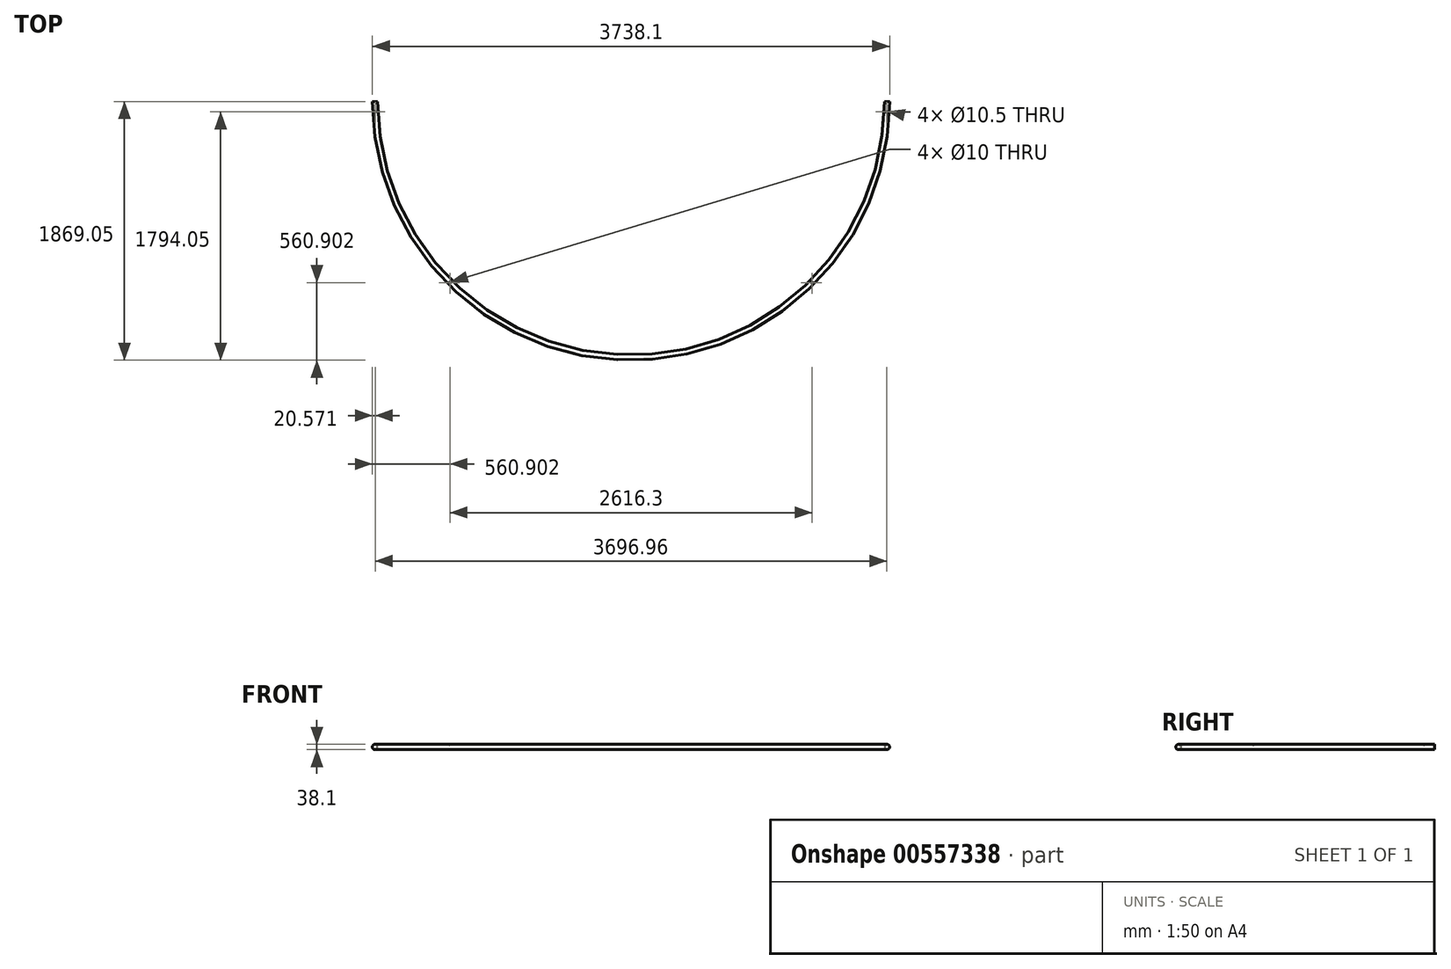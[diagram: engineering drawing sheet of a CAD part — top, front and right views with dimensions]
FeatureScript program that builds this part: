
annotation { "Feature Type Name" : "Feature", "Feature Type Description" : "" }
export const myFeature = defineFeature(function(context is Context, id is Id, definition is map)
    precondition{}
    {
        {
            var Q0;
            Q0=qCreatedBy(makeId("Front.planeOp"),FACE);
            var sketch = newSketch(context, id + "F0", { "sketchPlane" : qUnion([Q0])});
            skCircle(sketch, "E0", {"center": v(-1850, 0) * mm, "radius": 19.05 * mm});
            skCircle(sketch, "E1", {"center": v(-1850, 0) * mm, "radius": 15.85 * mm});
            skLineSegment(sketch, "E2", {"start": v(0, 0) * mm, "end": v(0, 380.17) * mm, "construction": true});
            skSolve(sketch);
        }
        {
            var Q0;
            Q0 = qSketchRegion(id + "F0", true);
            var Q1;
            Q1=sQuery(id+"F0.wireOp",EDGE,"E2");
            revolve(context, id + "F1", {"entities" : qUnion([Q0]), "axis" : qUnion([Q1]), "revolveType" : RevolveType.ONE_DIRECTION, "angle" : 180 * degree});
        }
        {
            var Q0;
            Q0=qCreatedBy(makeId("Top.planeOp"),FACE);
            var sketch = newSketch(context, id + "F2", { "sketchPlane" : qUnion([Q0])});
            skArc(sketch, "E3", {"start": v(-1850, 0) * mm, "mid": v(0, -1850) * mm, "end": v(1850, 0) * mm, "construction": true});
            skCircle(sketch, "E4", {"center": v(-1848.48, -75) * mm, "radius": 5.25 * mm});
            skLineSegment(sketch, "E5", {"start": v(0, 0) * mm, "end": v(0, -1850) * mm, "construction": true});
            skCircle(sketch, "E6.MirrorC", {"center": v(1848.48, -75) * mm, "radius": 5.25 * mm});
            skSolve(sketch);
        }
        {
            var Q0;
            Q0 = qSketchRegion(id + "F2", true);
            extrude(context, id + "F3", {"entities" : qUnion([Q0]), "operationType" : NewBodyOperationType.REMOVE, "endBound" : BoundingType.THROUGH_ALL, "oppositeDirection" : true, "depth" : 25 * mm, "offsetDistance" : 25 * mm, "hasSecondDirection" : true, "secondDirectionBound" : BoundingType.THROUGH_ALL, "secondDirectionOppositeDirection" : false, "secondDirectionDepth" : 25 * mm});
        }
        {
            var Q0;
            Q0=qCreatedBy(makeId("Top.planeOp"),FACE);
            var sketch = newSketch(context, id + "F4", { "sketchPlane" : qUnion([Q0])});
            skCircle(sketch, "E7", {"center": v(-1308.15, -1308.15) * mm, "radius": 5 * mm});
            skLineSegment(sketch, "E8", {"start": v(-1308.15, -1308.15) * mm, "end": v(0, 0) * mm, "construction": true});
            skCircle(sketch, "E9.MirrorC", {"center": v(1308.15, -1308.15) * mm, "radius": 5 * mm});
            skSolve(sketch);
        }
        {
            var Q0;
            Q0 = qSketchRegion(id + "F4", true);
            extrude(context, id + "F5", {"entities" : qUnion([Q0]), "operationType" : NewBodyOperationType.REMOVE, "endBound" : BoundingType.THROUGH_ALL, "depth" : 25 * mm, "offsetDistance" : 25 * mm, "hasSecondDirection" : true, "secondDirectionBound" : BoundingType.THROUGH_ALL, "secondDirectionOppositeDirection" : true, "secondDirectionDepth" : 25 * mm});
        }
    });
